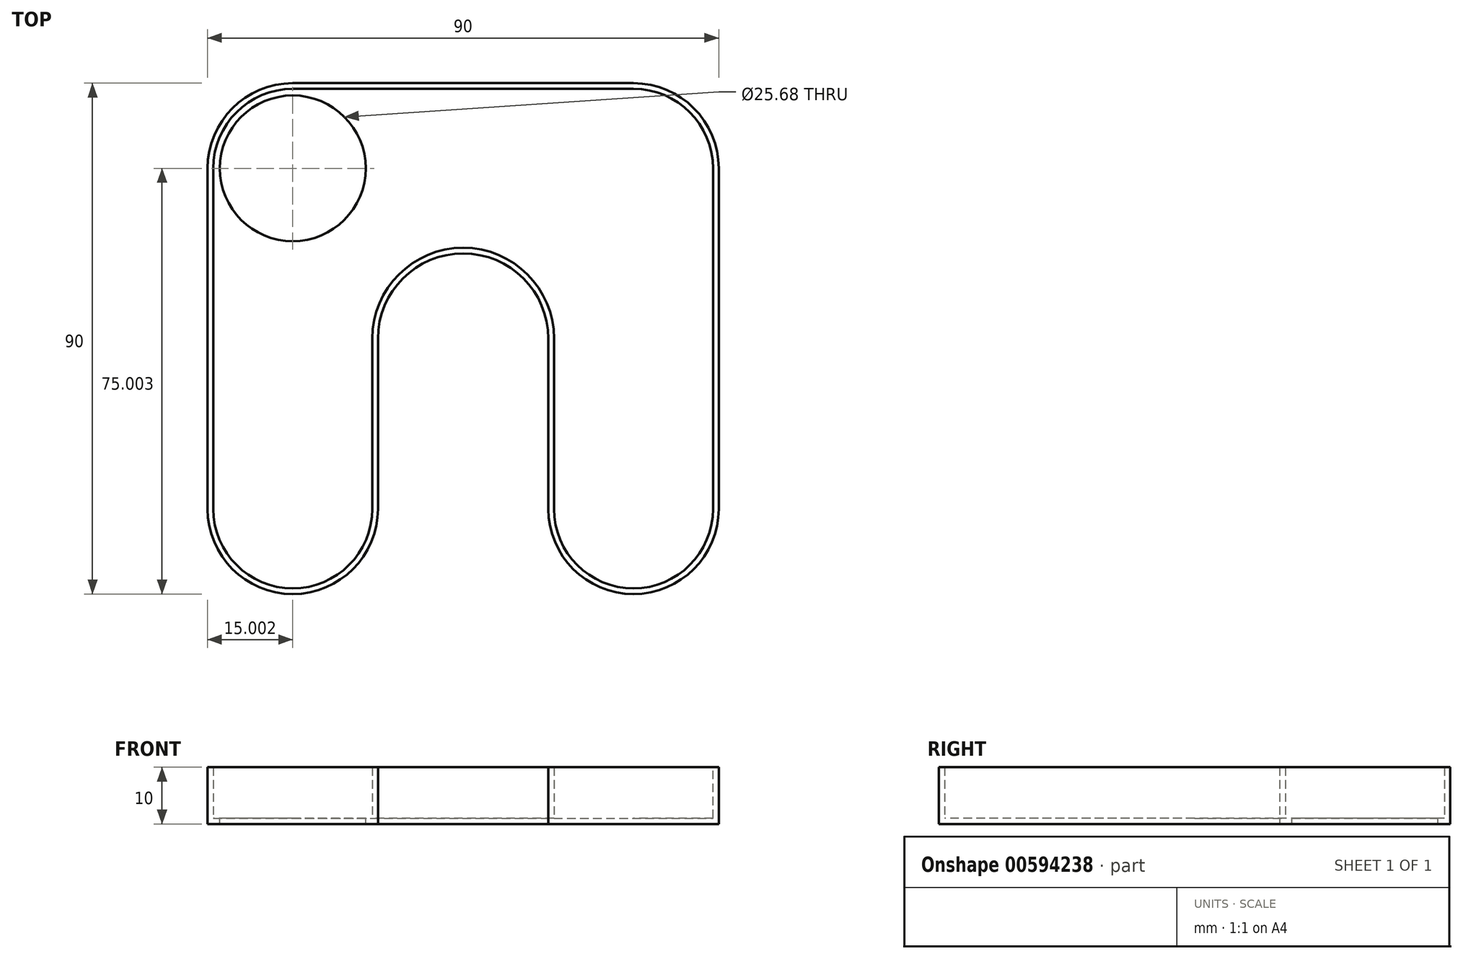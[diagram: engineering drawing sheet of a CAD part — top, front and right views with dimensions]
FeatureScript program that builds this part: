
annotation { "Feature Type Name" : "Feature", "Feature Type Description" : "" }
export const myFeature = defineFeature(function(context is Context, id is Id, definition is map)
    precondition{}
    {
        {
            var Q0;
            Q0=qCreatedBy(makeId("Top.planeOp"),FACE);
            var sketch = newSketch(context, id + "F0", { "sketchPlane" : qUnion([Q0])});
            skLineSegment(sketch, "E0.bottom", {"start": v(-64.19, 34.17) * mm, "end": v(-4.19, 34.17) * mm});
            skLineSegment(sketch, "E0.top", {"start": v(-64.19, -55.83) * mm, "end": v(-64.19, -55.83) * mm});
            skLineSegment(sketch, "E0.left", {"start": v(-79.19, 19.17) * mm, "end": v(-79.19, -40.83) * mm});
            skLineSegment(sketch, "E0.right", {"start": v(10.81, 19.17) * mm, "end": v(10.81, -40.83) * mm});
            skLineSegment(sketch, "E1.bottom", {"start": v(-34.19, 4.17) * mm, "end": v(-34.19, 4.17) * mm});
            skLineSegment(sketch, "E1.left", {"start": v(-49.19, -10.83) * mm, "end": v(-49.19, -40.83) * mm});
            skLineSegment(sketch, "E1.right", {"start": v(-19.19, -10.83) * mm, "end": v(-19.19, -40.83) * mm});
            skLineSegment(sketch, "E2.trimOffspring", {"start": v(-4.19, -55.83) * mm, "end": v(-4.19, -55.83) * mm});
            skPoint(sketch, "E3.visualSharp", {"position": v(-79.19, 34.17) * mm});
            skArc(sketch, "E3.filletArc", {"start": v(-64.19, 34.17) * mm, "mid": v(-74.8, 29.78) * mm, "end": v(-79.19, 19.17) * mm});
            skPoint(sketch, "E4.visualSharp", {"position": v(10.81, 34.17) * mm});
            skArc(sketch, "E4.filletArc", {"start": v(10.81, 19.17) * mm, "mid": v(6.42, 29.78) * mm, "end": v(-4.19, 34.17) * mm});
            skPoint(sketch, "E5.visualSharp", {"position": v(-79.19, -55.83) * mm});
            skArc(sketch, "E5.filletArc", {"start": v(-79.19, -40.83) * mm, "mid": v(-74.8, -51.43) * mm, "end": v(-64.19, -55.83) * mm});
            skPoint(sketch, "E6.visualSharp", {"position": v(-49.19, -55.83) * mm});
            skArc(sketch, "E6.filletArc", {"start": v(-64.19, -55.83) * mm, "mid": v(-53.58, -51.43) * mm, "end": v(-49.19, -40.83) * mm});
            skPoint(sketch, "E7.visualSharp", {"position": v(-49.19, 4.17) * mm});
            skArc(sketch, "E7.filletArc", {"start": v(-34.19, 4.17) * mm, "mid": v(-44.8, -0.22) * mm, "end": v(-49.19, -10.83) * mm});
            skPoint(sketch, "E8.visualSharp", {"position": v(-19.19, 4.17) * mm});
            skArc(sketch, "E8.filletArc", {"start": v(-19.19, -10.83) * mm, "mid": v(-23.58, -0.22) * mm, "end": v(-34.19, 4.17) * mm});
            skPoint(sketch, "E9.visualSharp", {"position": v(-19.19, -55.83) * mm});
            skArc(sketch, "E9.filletArc", {"start": v(-19.19, -40.83) * mm, "mid": v(-14.8, -51.43) * mm, "end": v(-4.19, -55.83) * mm});
            skPoint(sketch, "E10.visualSharp", {"position": v(10.81, -55.83) * mm});
            skArc(sketch, "E10.filletArc", {"start": v(-4.19, -55.83) * mm, "mid": v(6.42, -51.43) * mm, "end": v(10.81, -40.83) * mm});
            skSolve(sketch);
        }
        {
            var Q0;
            Q0 = qSketchRegion(id + "F0", true);
            extrude(context, id + "F1", {"entities" : qUnion([Q0]), "depth" : 10 * mm, "offsetDistance" : 25 * mm});
        }
        {
            var Q0;
            Q0=makeQuery(id+"F1.opExtrude","CAP_FACE",FACE,{"disambiguationData":[OSD([sQuery(id+"F0.wireOp",EDGE,"E0.bottom"),sQuery(id+"F0.wireOp",EDGE,"E0.left"),sQuery(id+"F0.wireOp",EDGE,"E0.right"),sQuery(id+"F0.wireOp",EDGE,"E1.left"),sQuery(id+"F0.wireOp",EDGE,"E1.right"),sQuery(id+"F0.wireOp",EDGE,"E3.filletArc"),sQuery(id+"F0.wireOp",EDGE,"E4.filletArc"),sQuery(id+"F0.wireOp",EDGE,"E5.filletArc"),sQuery(id+"F0.wireOp",EDGE,"E6.filletArc"),sQuery(id+"F0.wireOp",EDGE,"E7.filletArc"),sQuery(id+"F0.wireOp",EDGE,"E8.filletArc"),sQuery(id+"F0.wireOp",EDGE,"E9.filletArc"),sQuery(id+"F0.wireOp",EDGE,"E10.filletArc")])],"isStart":false});
            shell(context, id + "F2", {"entities" : qUnion([Q0]), "thickness" : 1 * mm});
        }
        {
            var Q0;
            Q0=makeQuery(id+"F2.opShell","OFFSET_FACE",FACE,{"disambiguationData":[OSD([sQuery(id+"F0.wireOp",EDGE,"E0.bottom"),sQuery(id+"F0.wireOp",EDGE,"E0.left"),sQuery(id+"F0.wireOp",EDGE,"E0.right"),sQuery(id+"F0.wireOp",EDGE,"E1.left"),sQuery(id+"F0.wireOp",EDGE,"E1.right"),sQuery(id+"F0.wireOp",EDGE,"E3.filletArc"),sQuery(id+"F0.wireOp",EDGE,"E4.filletArc"),sQuery(id+"F0.wireOp",EDGE,"E5.filletArc"),sQuery(id+"F0.wireOp",EDGE,"E6.filletArc"),sQuery(id+"F0.wireOp",EDGE,"E7.filletArc"),sQuery(id+"F0.wireOp",EDGE,"E8.filletArc"),sQuery(id+"F0.wireOp",EDGE,"E9.filletArc"),sQuery(id+"F0.wireOp",EDGE,"E10.filletArc")])]});
            var sketch = newSketch(context, id + "F3", { "sketchPlane" : qUnion([Q0])});
            skCircle(sketch, "E11", {"center": v(-64.19, 19.17) * mm, "radius": 12.84 * mm});
            skSolve(sketch);
        }
        {
            var Q0;
            Q0=makeQuery(id+"F3.imprint","IMPRINT",FACE,{"disambiguationData":[TD([[makeQuery(id+"F3.imprint","IMPRINT",EDGE,{"derivedFrom":sQuery(id+"F3.wireOp",EDGE,"E11")}),1.0]])]});
            extrude(context, id + "F4", {"entities" : qUnion([Q0]), "operationType" : NewBodyOperationType.REMOVE, "oppositeDirection" : true, "depth" : 25 * mm, "offsetDistance" : 25 * mm});
        }
    });
